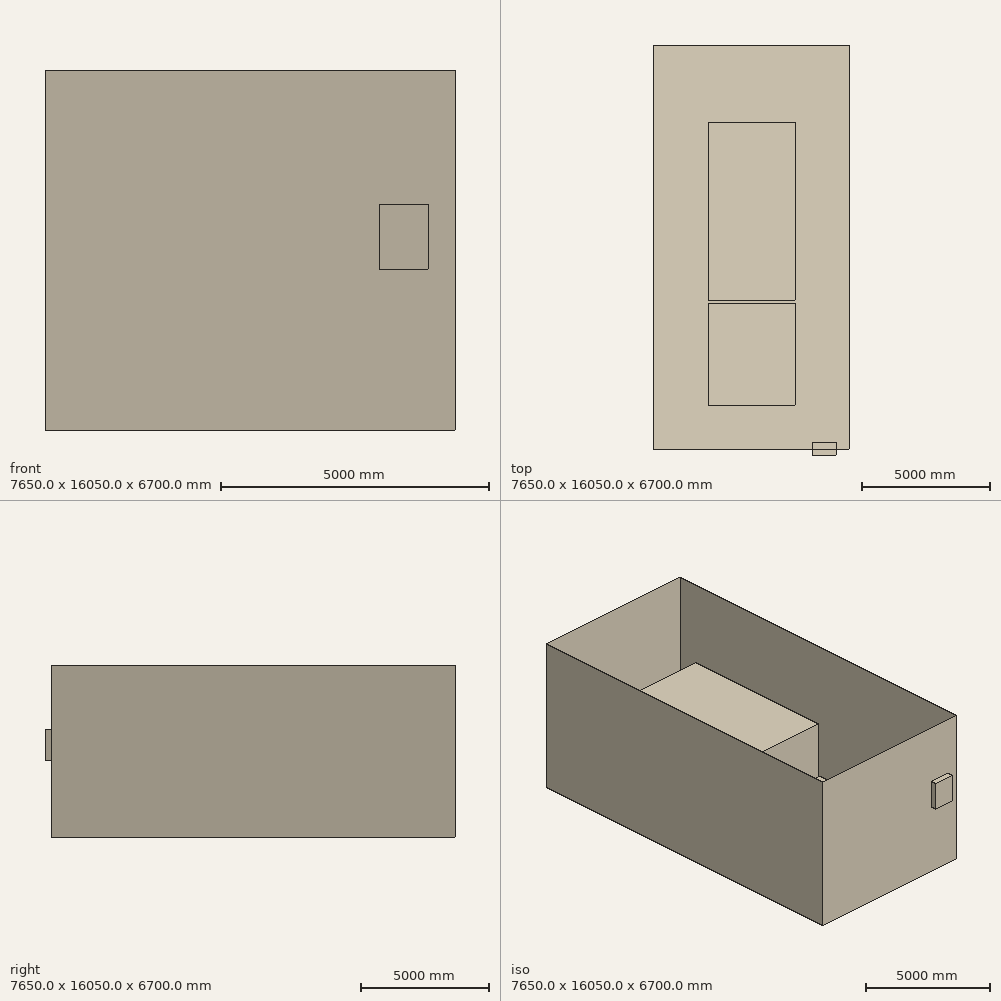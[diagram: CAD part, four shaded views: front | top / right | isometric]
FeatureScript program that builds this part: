
annotation { "Feature Type Name" : "Feature", "Feature Type Description" : "" }
export const myFeature = defineFeature(function(context is Context, id is Id, definition is map)
    precondition{}
    {
        {
            var Q0;
            Q0=qCreatedBy(makeId("Top.planeOp"),FACE);
            var sketch = newSketch(context, id + "F0", { "sketchPlane" : qUnion([Q0])});
            skLineSegment(sketch, "E0.bottom", {"start": v(2578.99, -7898.02) * mm, "end": v(-5071.01, -7898.02) * mm});
            skLineSegment(sketch, "E0.top", {"start": v(2578.99, 7901.98) * mm, "end": v(-5071.01, 7901.98) * mm});
            skLineSegment(sketch, "E0.left", {"start": v(2578.99, -7898.02) * mm, "end": v(2578.99, 7901.98) * mm});
            skLineSegment(sketch, "E0.right", {"start": v(-5071.01, -7898.02) * mm, "end": v(-5071.01, 7901.98) * mm});
            skSolve(sketch);
        }
        {
            var Q0;
            Q0=makeQuery(id+"F0.imprint","IMPRINT",FACE,{"disambiguationData":[TD([[makeQuery(id+"F0.imprint","IMPRINT",EDGE,{"derivedFrom":sQuery(id+"F0.wireOp",EDGE,"E0.bottom")}),-1.0]])]});
            extrude(context, id + "F1", {"entities" : qUnion([Q0]), "depth" : 6700 * mm});
        }
        {
            var Q0;
            Q0=makeQuery(id+"F1.opExtrude","CAP_FACE",FACE,{"disambiguationData":[OSD([sQuery(id+"F0.wireOp",EDGE,"E0.bottom"),sQuery(id+"F0.wireOp",EDGE,"E0.top"),sQuery(id+"F0.wireOp",EDGE,"E0.left"),sQuery(id+"F0.wireOp",EDGE,"E0.right")])],"isStart":false});
            shell(context, id + "F2", {"entities" : qUnion([Q0]), "thickness" : 2.5 * mm});
        }
        {
            var Q0;
            Q0=makeQuery(id+"F2.opShell","OFFSET_FACE",FACE,{"disambiguationData":[OSD([sQuery(id+"F0.wireOp",EDGE,"E0.bottom"),sQuery(id+"F0.wireOp",EDGE,"E0.top"),sQuery(id+"F0.wireOp",EDGE,"E0.left"),sQuery(id+"F0.wireOp",EDGE,"E0.right")])]});
            var sketch = newSketch(context, id + "F3", { "sketchPlane" : qUnion([Q0])});
            skLineSegment(sketch, "E1.bottom", {"start": v(478.99, 4901.98) * mm, "end": v(-2921.01, 4901.98) * mm});
            skLineSegment(sketch, "E1.top", {"start": v(478.99, -2098.02) * mm, "end": v(-2921.01, -2098.02) * mm});
            skLineSegment(sketch, "E1.left", {"start": v(478.99, 4901.98) * mm, "end": v(478.99, -2098.02) * mm});
            skLineSegment(sketch, "E1.right", {"start": v(-2921.01, 4901.98) * mm, "end": v(-2921.01, -2098.02) * mm});
            skLineSegment(sketch, "E2.bottom", {"start": v(478.99, -2198.02) * mm, "end": v(-2921.01, -2198.02) * mm});
            skLineSegment(sketch, "E2.top", {"start": v(478.99, -6198.02) * mm, "end": v(-2921.01, -6198.02) * mm});
            skLineSegment(sketch, "E2.left", {"start": v(478.99, -2198.02) * mm, "end": v(478.99, -6198.02) * mm});
            skLineSegment(sketch, "E2.right", {"start": v(-2921.01, -2198.02) * mm, "end": v(-2921.01, -6198.02) * mm});
            skSolve(sketch);
        }
        {
            var Q0;
            Q0=makeQuery(id+"F3.imprint","IMPRINT",FACE,{"disambiguationData":[TD([[makeQuery(id+"F3.imprint","IMPRINT",EDGE,{"derivedFrom":sQuery(id+"F3.wireOp",EDGE,"E1.bottom")}),1.0]])]});
            extrude(context, id + "F4", {"entities" : qUnion([Q0]), "operationType" : NewBodyOperationType.ADD, "depth" : 4780 * mm});
        }
        {
            var Q0;
            Q0 = qSketchRegion(id + "F3", true);
            extrude(context, id + "F5", {"entities" : qUnion([Q0]), "operationType" : NewBodyOperationType.ADD, "depth" : 2385 * mm});
        }
        {
            var Q0;
            Q0=makeQuery(id+"F1.opExtrude","SWEPT_FACE",FACE,{"disambiguationData":[OSD([sQuery(id+"F0.wireOp",EDGE,"E0.bottom")])]});
            var sketch = newSketch(context, id + "F6", { "sketchPlane" : qUnion([Q0])});
            skLineSegment(sketch, "E3.bottom", {"start": v(-4571.01, 4200) * mm, "end": v(-3646.01, 4200) * mm});
            skLineSegment(sketch, "E3.top", {"start": v(-4571.01, 3000) * mm, "end": v(-3646.01, 3000) * mm});
            skLineSegment(sketch, "E3.left", {"start": v(-4571.01, 4200) * mm, "end": v(-4571.01, 3000) * mm});
            skLineSegment(sketch, "E3.right", {"start": v(-3646.01, 4200) * mm, "end": v(-3646.01, 3000) * mm});
            skLineSegment(sketch, "E4.bottom", {"start": v(1153.99, 4200) * mm, "end": v(2078.99, 4200) * mm});
            skLineSegment(sketch, "E4.top", {"start": v(1153.99, 3000) * mm, "end": v(2078.99, 3000) * mm});
            skLineSegment(sketch, "E4.left", {"start": v(1153.99, 4200) * mm, "end": v(1153.99, 3000) * mm});
            skLineSegment(sketch, "E4.right", {"start": v(2078.99, 4200) * mm, "end": v(2078.99, 3000) * mm});
            skSolve(sketch);
        }
        {
            var Q0;
            Q0=makeQuery(id+"F6.imprint","IMPRINT",FACE,{"disambiguationData":[TD([[makeQuery(id+"F6.imprint","IMPRINT",EDGE,{"derivedFrom":sQuery(id+"F6.wireOp",EDGE,"E4.bottom")}),-1.0]])]});
            extrude(context, id + "F7", {"entities" : qUnion([Q0]), "operationType" : NewBodyOperationType.ADD, "endBound" : BoundingType.SYMMETRIC, "depth" : 500 * mm});
        }
    });
